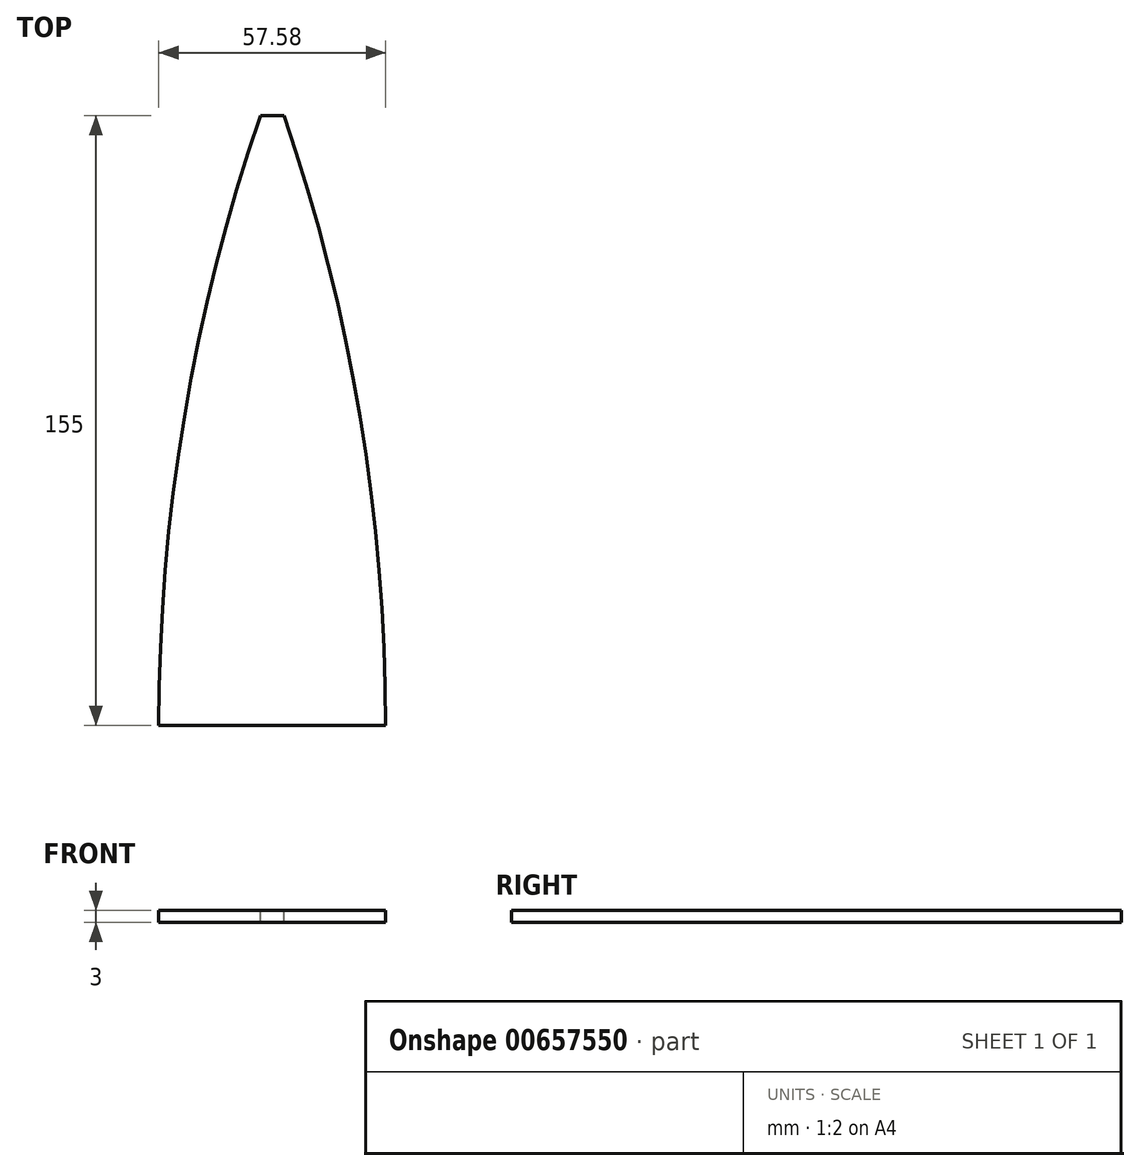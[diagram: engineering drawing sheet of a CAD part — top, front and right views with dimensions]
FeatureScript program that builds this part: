
annotation { "Feature Type Name" : "Feature", "Feature Type Description" : "" }
export const myFeature = defineFeature(function(context is Context, id is Id, definition is map)
    precondition{}
    {
        {
            var Q0;
            Q0=qCreatedBy(makeId("Top.planeOp"),FACE);
            var sketch = newSketch(context, id + "F0", { "sketchPlane" : qUnion([Q0])});
            skLineSegment(sketch, "E0.bottom", {"start": v(-28.83, 0) * mm, "end": v(28.83, 0) * mm, "construction": true});
            skLineSegment(sketch, "E0.top", {"start": v(-28.83, 155) * mm, "end": v(28.83, 155) * mm, "construction": true});
            skLineSegment(sketch, "E0.left", {"start": v(-28.83, 0) * mm, "end": v(-28.83, 155) * mm, "construction": true});
            skLineSegment(sketch, "E0.right", {"start": v(28.83, 0) * mm, "end": v(28.83, 155) * mm, "construction": true});
            skLineSegment(sketch, "E1", {"start": v(0, 0) * mm, "end": v(0, 155) * mm});
            skLineSegment(sketch, "E2", {"start": v(-3, 155) * mm, "end": v(-28.83, 0) * mm, "construction": true});
            skLineSegment(sketch, "E3", {"start": v(3, 155) * mm, "end": v(28.83, 0) * mm, "construction": true});
            skLineSegment(sketch, "E4", {"start": v(-15.92, 77.5) * mm, "end": v(654.75, -34.28) * mm, "construction": true});
            skLineSegment(sketch, "E5", {"start": v(-28.83, 0) * mm, "end": v(780.18, 0) * mm, "construction": true});
            skLineSegment(sketch, "E6", {"start": v(780.18, 0) * mm, "end": v(-898.14, 0) * mm, "construction": true});
            skLineSegment(sketch, "E7", {"start": v(15.92, 77.5) * mm, "end": v(-534, -14.15) * mm, "construction": true});
            skPoint(sketch, "E7.startSnap0", {"position": v(0, 77.5) * mm});
            skLineSegment(sketch, "E8", {"start": v(0, 135.26) * mm, "end": v(0, 184.4) * mm, "construction": true});
            skArc(sketch, "E9", {"start": v(-28.83, 0) * mm, "mid": v(-21.57, 83) * mm, "end": v(0, 163.49) * mm});
            skSolve(sketch);
        }
        {
            var Q0;
            Q0=qCreatedBy(makeId("Top.planeOp"),FACE);
            var sketch = newSketch(context, id + "F1", { "sketchPlane" : qUnion([Q0])});
            skArc(sketch, "E10", {"start": v(28.76, 0) * mm, "mid": v(22.28, 78.56) * mm, "end": v(3, 155) * mm});
            skArc(sketch, "E11", {"start": v(-28.82, 0) * mm, "mid": v(-22.32, 78.57) * mm, "end": v(-3, 155) * mm});
            skLineSegment(sketch, "E12", {"start": v(-28.82, 0) * mm, "end": v(28.76, 0) * mm});
            skLineSegment(sketch, "E13", {"start": v(-3, 155) * mm, "end": v(3, 155) * mm});
            skSolve(sketch);
        }
        {
            var Q0;
            Q0=makeQuery(id+"F1.imprint","IMPRINT",FACE,{"disambiguationData":[TD([[makeQuery(id+"F1.imprint","IMPRINT",EDGE,{"derivedFrom":sQuery(id+"F1.wireOp",EDGE,"E10")}),1.0]])]});
            extrude(context, id + "F2", {"entities" : qUnion([Q0]), "oppositeDirection" : true, "depth" : 3 * mm, "offsetDistance" : 25 * mm});
        }
    });
